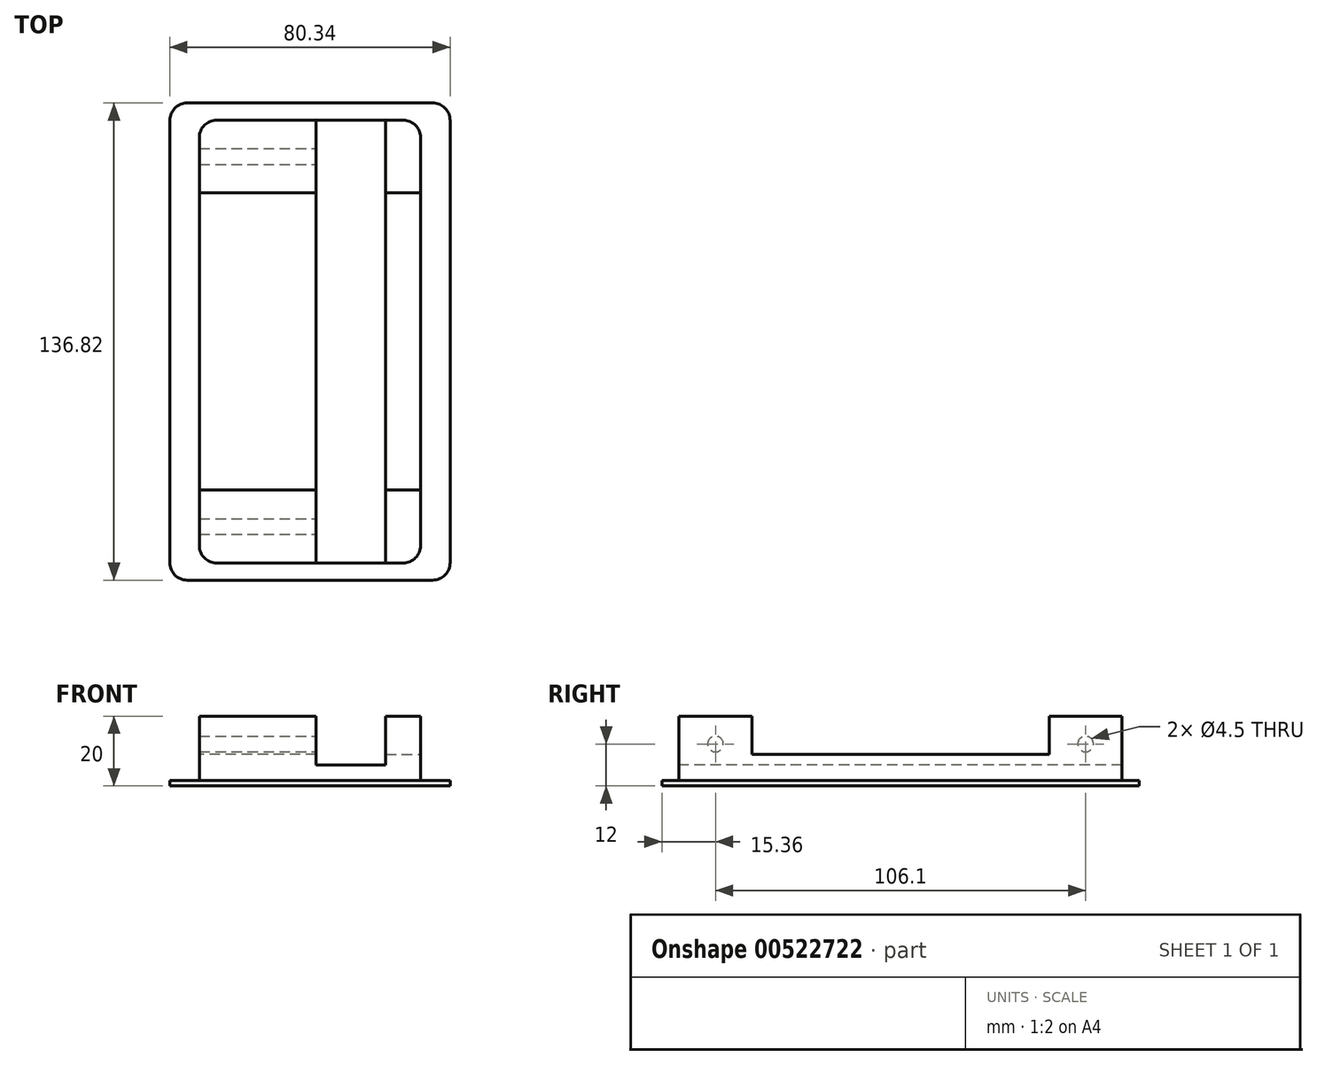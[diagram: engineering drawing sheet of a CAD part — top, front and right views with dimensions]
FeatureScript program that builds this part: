
annotation { "Feature Type Name" : "Feature", "Feature Type Description" : "" }
export const myFeature = defineFeature(function(context is Context, id is Id, definition is map)
    precondition{}
    {
        {
            var Q0;
            Q0=qCreatedBy(makeId("Top.planeOp"),FACE);
            var sketch = newSketch(context, id + "F0", { "sketchPlane" : qUnion([Q0])});
            skLineSegment(sketch, "E0.bottom", {"start": v(12, 63.5) * mm, "end": v(-12, 63.5) * mm});
            skLineSegment(sketch, "E0.top", {"start": v(12, -63.5) * mm, "end": v(-12, -63.5) * mm});
            skLineSegment(sketch, "E0.left", {"start": v(12, 63.5) * mm, "end": v(12, -63.5) * mm});
            skLineSegment(sketch, "E0.right", {"start": v(-12, 63.5) * mm, "end": v(-12, -63.5) * mm});
            skPoint(sketch, "E0.middle", {"position": v(0, 0) * mm});
            skSolve(sketch);
        }
        {
            var Q0;
            Q0=qSketchRegion(id+"F0",true);
            extrude(context, id + "F1", {"entities" : qUnion([Q0]), "depth" : 33.5 * mm, "offsetDistance" : 25 * mm});
        }
        {
            var Q0;
            Q0=makeQuery(id+"F1.opExtrude","CAP_FACE",FACE,{"disambiguationData":[OSD([sQuery(id+"F0.wireOp",EDGE,"E0.bottom"),sQuery(id+"F0.wireOp",EDGE,"E0.top"),sQuery(id+"F0.wireOp",EDGE,"E0.left"),sQuery(id+"F0.wireOp",EDGE,"E0.right")])],"isStart":false});
            var sketch = newSketch(context, id + "F2", { "sketchPlane" : qUnion([Q0])});
            skLineSegment(sketch, "E1.bottom", {"start": v(12, 63.5) * mm, "end": v(6, 63.5) * mm});
            skLineSegment(sketch, "E1.top", {"start": v(12, -63.5) * mm, "end": v(6, -63.5) * mm});
            skLineSegment(sketch, "E1.left", {"start": v(12, 63.5) * mm, "end": v(12, -63.5) * mm});
            skLineSegment(sketch, "E1.right", {"start": v(6, 63.5) * mm, "end": v(6, -63.5) * mm});
            skSolve(sketch);
        }
        {
            var Q0;
            Q0=qSketchRegion(id+"F2",true);
            extrude(context, id + "F3", {"entities" : qUnion([Q0]), "operationType" : NewBodyOperationType.ADD, "depth" : 19.9 * mm, "offsetDistance" : 25 * mm});
        }
        {
            var Q0;
            Q0=makeQuery(id+"F1.opExtrude","CAP_FACE",FACE,{"disambiguationData":[OSD([sQuery(id+"F0.wireOp",EDGE,"E0.bottom"),sQuery(id+"F0.wireOp",EDGE,"E0.top"),sQuery(id+"F0.wireOp",EDGE,"E0.left"),sQuery(id+"F0.wireOp",EDGE,"E0.right")])],"isStart":false});
            var sketch = newSketch(context, id + "F4", { "sketchPlane" : qUnion([Q0])});
            skCircle(sketch, "E2", {"center": v(0, 53.05) * mm, "radius": 2.25 * mm});
            skCircle(sketch, "E3", {"center": v(0, -53.05) * mm, "radius": 2.25 * mm});
            skLineSegment(sketch, "E4", {"start": v(0, 63.5) * mm, "end": v(0, 55.3) * mm, "construction": true});
            skLineSegment(sketch, "E5", {"start": v(0, -55.3) * mm, "end": v(0, -63.5) * mm, "construction": true});
            skSolve(sketch);
        }
        {
            var Q0;
            Q0=makeQuery(id+"F3.opExtrude","CAP_FACE",FACE,{"disambiguationData":[OSD([sQuery(id+"F2.wireOp",EDGE,"E1.bottom"),sQuery(id+"F2.wireOp",EDGE,"E1.top"),sQuery(id+"F2.wireOp",EDGE,"E1.left"),sQuery(id+"F2.wireOp",EDGE,"E1.right")])],"isStart":false});
            var sketch = newSketch(context, id + "F5", { "sketchPlane" : qUnion([Q0])});
            skPoint(sketch, "E6.0", {"position": v(-12, -63.5) * mm});
            skPoint(sketch, "E6.1", {"position": v(-12, 63.5) * mm});
            skLineSegment(sketch, "E7.bottom", {"start": v(12, 63.5) * mm, "end": v(-12, 63.5) * mm});
            skLineSegment(sketch, "E7.top", {"start": v(12, -63.5) * mm, "end": v(-12, -63.5) * mm});
            skLineSegment(sketch, "E7.left", {"start": v(12, 63.5) * mm, "end": v(12, -63.5) * mm});
            skLineSegment(sketch, "E7.right", {"start": v(-12, 63.5) * mm, "end": v(-12, -63.5) * mm});
            skSolve(sketch);
        }
        {
            var Q0;
            Q0 = qSketchRegion(id + "F5", true);
            extrude(context, id + "F6", {"entities" : qUnion([Q0]), "operationType" : NewBodyOperationType.ADD, "depth" : 10 * mm, "offsetDistance" : 25 * mm});
        }
        {
            var Q0;
            Q0=makeQuery(id+"F1.opExtrude","SWEPT_FACE",FACE,{"disambiguationData":[OSD([sQuery(id+"F0.wireOp",EDGE,"E0.right")])]});
            var sketch = newSketch(context, id + "F7", { "sketchPlane" : qUnion([Q0])});
            skLineSegment(sketch, "E8.0", {"start": v(-42.6, 33.5) * mm, "end": v(42.6, 33.5) * mm});
            skLineSegment(sketch, "E8.1", {"start": v(-42.6, 0) * mm, "end": v(42.6, 0) * mm});
            skLineSegment(sketch, "E8.2", {"start": v(-63.5, 33.5) * mm, "end": v(-63.5, 0) * mm, "construction": true});
            skLineSegment(sketch, "E8.3", {"start": v(63.5, 33.5) * mm, "end": v(63.5, 0) * mm, "construction": true});
            skLineSegment(sketch, "E9.left", {"start": v(-42.6, 33.5) * mm, "end": v(-42.6, 0) * mm});
            skLineSegment(sketch, "E9.right", {"start": v(42.6, 33.5) * mm, "end": v(42.6, 0) * mm});
            skLineSegment(sketch, "E10", {"start": v(-63.5, 33.5) * mm, "end": v(-42.6, 33.5) * mm, "construction": true});
            skLineSegment(sketch, "E11", {"start": v(42.6, 33.5) * mm, "end": v(63.5, 33.5) * mm, "construction": true});
            skLineSegment(sketch, "E12.0", {"start": v(-63.5, 63.4) * mm, "end": v(63.5, 63.4) * mm, "construction": true});
            skLineSegment(sketch, "E12.1", {"start": v(-63.5, 53.4) * mm, "end": v(63.5, 53.4) * mm, "construction": true});
            skLineSegment(sketch, "E13", {"start": v(-42.6, 53.4) * mm, "end": v(-42.6, 63.4) * mm});
            skLineSegment(sketch, "E14", {"start": v(-42.6, 63.4) * mm, "end": v(42.6, 63.4) * mm});
            skLineSegment(sketch, "E15", {"start": v(42.6, 63.4) * mm, "end": v(42.6, 53.4) * mm});
            skLineSegment(sketch, "E16", {"start": v(42.6, 53.4) * mm, "end": v(-42.6, 53.4) * mm});
            skSolve(sketch);
        }
        {
            var Q0;
            Q0 = qSketchRegion(id + "F7", true);
            extrude(context, id + "F8", {"entities" : qUnion([Q0]), "operationType" : NewBodyOperationType.REMOVE, "oppositeDirection" : true, "depth" : 15 * mm, "offsetDistance" : 25 * mm});
        }
        {
            var Q0;
            Q0=qSketchRegion(id+"F4",true);
            extrude(context, id + "F9", {"entities" : qUnion([Q0]), "operationType" : NewBodyOperationType.REMOVE, "endBound" : BoundingType.UP_TO_NEXT, "oppositeDirection" : true, "depth" : 25 * mm, "offsetDistance" : 25 * mm});
        }
        {
            var Q0;
            Q0=qCreatedBy(makeId("Top.planeOp"),FACE);
            var sketch = newSketch(context, id + "F10", { "sketchPlane" : qUnion([Q0])});
            skLineSegment(sketch, "E17", {"start": v(0, -74.27) * mm, "end": v(0, 69.8) * mm, "construction": true});
            skSolve(sketch);
        }
        {
            var Q0;
            Q0=makeQuery(id+"F1.opExtrude","SWEPT_BODY",BODY,{"disambiguationData":[OSD([sQuery(id+"F0.wireOp",EDGE,"E0.bottom"),sQuery(id+"F0.wireOp",EDGE,"E0.top"),sQuery(id+"F0.wireOp",EDGE,"E0.left"),sQuery(id+"F0.wireOp",EDGE,"E0.right")])]});
            var Q1;
            Q1=sQuery(id+"F10.wireOp",EDGE,"E17");
            transform(context, id + "F11", {"entities" : qUnion([Q0]), "transformType" : TransformType.ROTATION, "transformAxis" : qUnion([Q1]), "angle" : 90 * degree, "makeCopy" : false});
        }
        {
            var Q0;
            {var subQ0=sQuery(id+"F0.wireOp",EDGE,"E0.right");var subQ3=sQuery(id+"F0.wireOp",EDGE,"E0.bottom");Q0=makeQuery(id+"F8.boolean.opBoolean","SPLIT",FACE,{"disambiguationData":[TD([makeQuery(id+"F1.opExtrude","SWEPT_FACE",FACE,{"disambiguationData":[OSD([subQ3])]})])],"derivedFrom":makeQuery(id+"F1.opExtrude","SWEPT_FACE",FACE,{"disambiguationData":[OSD([subQ0])]})});}
            var sketch = newSketch(context, id + "F12", { "sketchPlane" : qUnion([Q0])});
            skPoint(sketch, "E18.0", {"position": v(63.4, -63.5) * mm});
            skPoint(sketch, "E18.1", {"position": v(0, 63.5) * mm});
            skLineSegment(sketch, "E19.bottom", {"start": v(0, 63.5) * mm, "end": v(63.4, 63.5) * mm});
            skLineSegment(sketch, "E19.top", {"start": v(0, -63.5) * mm, "end": v(63.4, -63.5) * mm});
            skLineSegment(sketch, "E19.left", {"start": v(0, 63.5) * mm, "end": v(0, -63.5) * mm});
            skLineSegment(sketch, "E19.right", {"start": v(63.4, 63.5) * mm, "end": v(63.4, -63.5) * mm});
            skSolve(sketch);
        }
        {
            var Q0;
            Q0 = qSketchRegion(id + "F12", true);
            extrude(context, id + "F13", {"entities" : qUnion([Q0]), "operationType" : NewBodyOperationType.REMOVE, "oppositeDirection" : true, "depth" : 4 * mm, "offsetDistance" : 25 * mm});
        }
        {
            var Q0;
            Q0=makeQuery(id+"F6.boolean.opBoolean","MERGE",FACE,{"derivedFrom":[makeQuery(id+"F3.boolean.opBoolean","MERGE",FACE,{"derivedFrom":[makeQuery(id+"F1.opExtrude","SWEPT_FACE",FACE,{"disambiguationData":[OSD([sQuery(id+"F0.wireOp",EDGE,"E0.left")])]}),makeQuery(id+"F3.opExtrude","SWEPT_FACE",FACE,{"disambiguationData":[OSD([sQuery(id+"F2.wireOp",EDGE,"E1.left")])]})]}),makeQuery(id+"F6.opExtrude","SWEPT_FACE",FACE,{"disambiguationData":[OSD([sQuery(id+"F5.wireOp",EDGE,"E7.left")])]})]});
            var sketch = newSketch(context, id + "F14", { "sketchPlane" : qUnion([Q0])});
            skLineSegment(sketch, "E20.bottom", {"start": v(71.87, 68.4) * mm, "end": v(-8.47, 68.4) * mm});
            skLineSegment(sketch, "E20.top", {"start": v(71.87, -68.4) * mm, "end": v(-8.47, -68.4) * mm});
            skLineSegment(sketch, "E20.left", {"start": v(71.87, 68.4) * mm, "end": v(71.87, -68.4) * mm});
            skLineSegment(sketch, "E20.right", {"start": v(-8.47, 68.4) * mm, "end": v(-8.47, -68.4) * mm});
            skPoint(sketch, "E20.middle", {"position": v(31.7, 0) * mm});
            skPoint(sketch, "E20.middle.positionSnap0", {"position": v(31.7, -63.5) * mm});
            skPoint(sketch, "E20.centerSnap0", {"position": v(31.7, -63.5) * mm});
            skSolve(sketch);
        }
        {
            var Q0;
            Q0 = qSketchRegion(id + "F14", true);
            extrude(context, id + "F15", {"entities" : qUnion([Q0]), "operationType" : NewBodyOperationType.ADD, "oppositeDirection" : true, "depth" : 1.5 * mm, "offsetDistance" : 25 * mm});
        }
        {
            var Q0;
            Q0=makeQuery(id+"F6.opExtrude","CAP_EDGE",EDGE,{"disambiguationData":[OSD([sQuery(id+"F5.wireOp",EDGE,"E7.bottom")])],"isStart":false});
            var Q1;
            Q1=makeQuery(id+"F1.opExtrude","CAP_EDGE",EDGE,{"disambiguationData":[OSD([sQuery(id+"F0.wireOp",EDGE,"E0.bottom")])],"isStart":true});
            var Q2;
            Q2=makeQuery(id+"F15.opExtrude","SWEPT_EDGE",EDGE,{"disambiguationData":[OSD([sQuery(id+"F14.wireOp",EDGE,"E20.top"),sQuery(id+"F14.wireOp",EDGE,"E20.right")])]});
            var Q3;
            Q3=makeQuery(id+"F15.opExtrude","SWEPT_EDGE",EDGE,{"disambiguationData":[OSD([sQuery(id+"F14.wireOp",EDGE,"E20.top"),sQuery(id+"F14.wireOp",EDGE,"E20.left")])]});
            var Q4;
            Q4=makeQuery(id+"F1.opExtrude","CAP_EDGE",EDGE,{"disambiguationData":[OSD([sQuery(id+"F0.wireOp",EDGE,"E0.top")])],"isStart":true});
            var Q5;
            Q5=makeQuery(id+"F6.opExtrude","CAP_EDGE",EDGE,{"disambiguationData":[OSD([sQuery(id+"F5.wireOp",EDGE,"E7.top")])],"isStart":false});
            var Q6;
            Q6=makeQuery(id+"F15.opExtrude","SWEPT_EDGE",EDGE,{"disambiguationData":[OSD([sQuery(id+"F14.wireOp",EDGE,"E20.bottom"),sQuery(id+"F14.wireOp",EDGE,"E20.left")])]});
            var Q7;
            Q7=makeQuery(id+"F15.opExtrude","SWEPT_EDGE",EDGE,{"disambiguationData":[OSD([sQuery(id+"F14.wireOp",EDGE,"E20.bottom"),sQuery(id+"F14.wireOp",EDGE,"E20.right")])]});
            fillet(context, id + "F16", {"entities" : qUnion([Q0, Q1, Q2, Q3, Q4, Q5, Q6, Q7]), "radius" : 5 * mm, "tangentPropagation" : true, "allowEdgeOverflow" : false});
        }
    });
